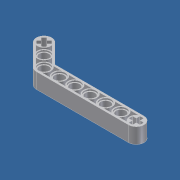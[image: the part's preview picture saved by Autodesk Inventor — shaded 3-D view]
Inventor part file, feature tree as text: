
AUTODESK INVENTOR PART (.ipt)
format: ipt  version: unknown  size: 437,248 bytes
history: native  units: mm
features: extrude x9, sketch x9
ambient origin geometry x8: Origin, YZ Plane, XZ Plane, XY Plane, X Axis, Y Axis, Z Axis, Center Point
bodies: Solid1 (feature_tree)
feature tree (18):
  extrude  "Extrusion1"  TaperAngle=0.0deg  [1 undecoded]
  extrude  "Extrusion2"  Depth=4.0mm
  extrude  "Extrusion3"  Depth=48.0mm
  extrude  "Extrusion4"  Depth=4.0mm
  extrude  "Extrusion5"  Depth=16.0mm
  extrude  "Extrusion6"  Depth=3.0mm
  extrude  "Extrusion7"  Depth=3.0mm
  extrude  "Extrusion8"  Depth=2.0mm
  extrude  "Extrusion9"  Depth=2.0mm
  sketch  "Sketch1"  dims[d13=4.0mm d15=0.0mm]
  sketch  "Sketch2"  dims[d16=0.0mm d25=4.0mm]
  sketch  "Sketch3"  dims[d27=135.0deg d29=48.0mm]
  sketch  "Sketch4"  dims[d35=135.0deg d36=4.0mm]
  sketch  "Sketch5"  dims[d37=16.0mm d38=16.0mm]
  sketch  "Sketch6"  dims[d39=8.0mm d40=0.0mm d46=3.0mm]
  sketch  "Sketch7"  dims[d47=3.0mm d48=3.0mm]
  sketch  "Sketch8"  dims[d49=3.0mm d50=2.0mm]
  sketch  "Sketch9"  dims[d51=2.0mm d52=2.0mm d53=2.0mm d54=1.0mm d55=1.0mm d56=1.0mm d57=1.0mm d58=90.0deg d59=90.0deg d60=90.0deg d61=90.0deg d62=8.0mm d63=0.0mm d64=6.0mm d65=3.0mm d66=3.0mm d67=3.0mm d68=3.0mm d69=2.0mm d70=2.0mm d71=2.0mm d72=2.0mm d73=90.0deg d74=90.0deg d75=90.0deg d76=1.0mm d77=1.0mm d78=1.0mm d79=1.0mm d80=2.828427mm d81=8.0mm d82=0.0mm d83=5.0mm d84=8.0mm d85=0.0mm d86=10.0mm d88=10.0mm d89=60.0mm d91=8.0mm d93=8.0mm d94=0.0mm d95=5.0mm d96=4.0mm d97=8.0mm d98=8.0mm d99=0.0mm d100=6.0mm d101=6.0mm d102=6.0mm d103=6.0mm d104=6.0mm d105=6.0mm d106=6.0mm d107=0.8mm d108=0.0mm d109=6.0mm d110=6.0mm d111=6.0mm d112=6.0mm d113=6.0mm d114=6.0mm d115=6.0mm d116=0.8mm d117=0.0mm d118=7.0mm d119=7.0mm d120=10.0mm d122=10.0mm d123=60.0mm d125=8.0mm d127=0.8mm d128=0.0mm d130=7.0mm d132=3.5mm d133=10.0mm d135=10.0mm d136=20.0mm d138=8.0mm d140=0.8mm d141=0.0mm]
note: 1 required parameter value undecoded (feature->parameter linkage not recoverable at this tier; creation-order binding heuristic only, values carry confidence <= 0.55)
